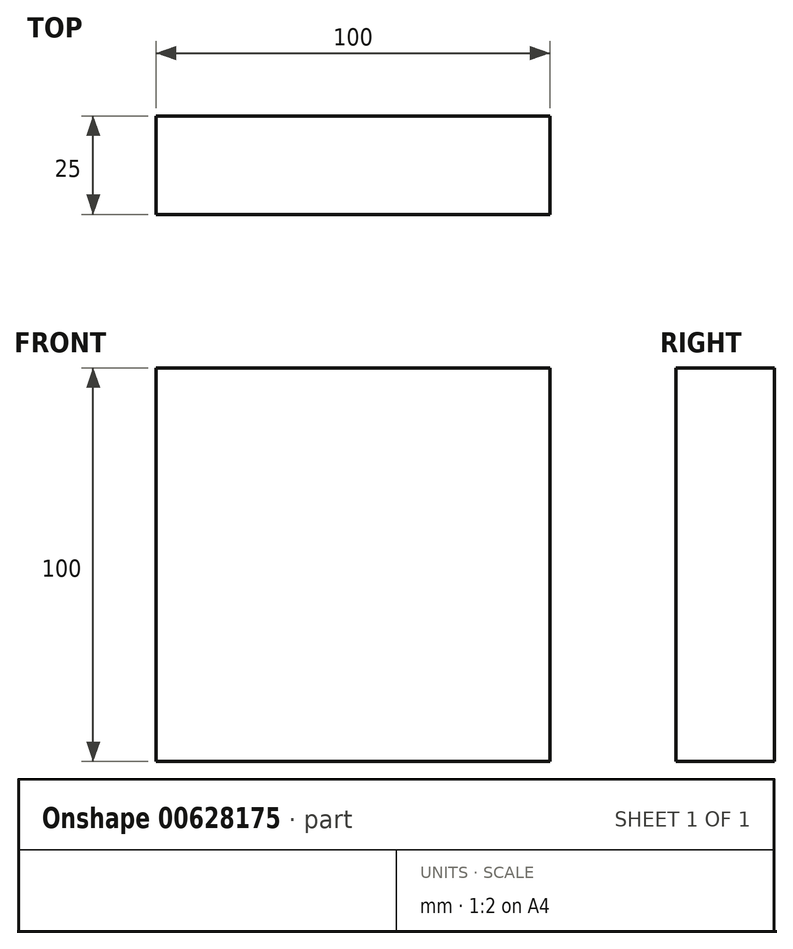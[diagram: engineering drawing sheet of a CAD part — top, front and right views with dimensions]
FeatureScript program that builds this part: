
annotation { "Feature Type Name" : "Feature", "Feature Type Description" : "" }
export const myFeature = defineFeature(function(context is Context, id is Id, definition is map)
    precondition{}
    {
        {
            var Q0;
            Q0=qCreatedBy(makeId("Front.planeOp"),FACE);
            var sketch = newSketch(context, id + "F0", { "sketchPlane" : qUnion([Q0])});
            skLineSegment(sketch, "E0.bottom", {"start": v(-50, 50) * mm, "end": v(50, 50) * mm});
            skLineSegment(sketch, "E0.top", {"start": v(-50, -50) * mm, "end": v(50, -50) * mm});
            skLineSegment(sketch, "E0.left", {"start": v(-50, 50) * mm, "end": v(-50, -50) * mm});
            skLineSegment(sketch, "E0.right", {"start": v(50, 50) * mm, "end": v(50, -50) * mm});
            skPoint(sketch, "E0.middle", {"position": v(0, 0) * mm});
            skSolve(sketch);
        }
        {
            var Q0;
            Q0 = qSketchRegion(id + "F0", true);
            extrude(context, id + "F1", {"entities" : qUnion([Q0]), "depth" : 25 * mm, "offsetDistance" : 25 * mm});
        }
    });
